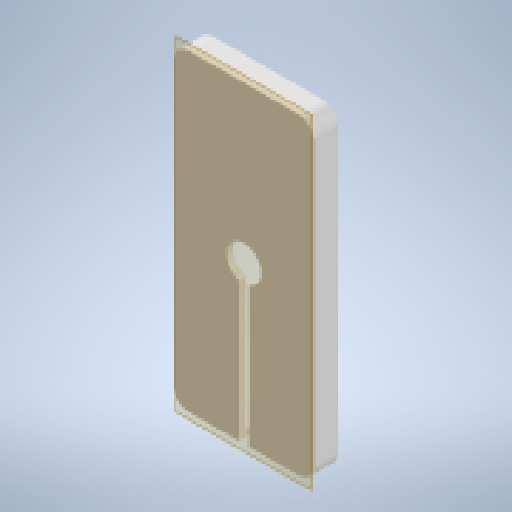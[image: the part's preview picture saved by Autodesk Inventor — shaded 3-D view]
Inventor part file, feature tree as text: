
AUTODESK INVENTOR PART (.ipt)
format: ipt  version: 2023 (Build 270158000, 158)  size: 202,752 bytes
history: native  units: mm
features: other x4, extrude x4, sketch x4, projected_geometry x3
ambient origin geometry x8: Origin, YZ Plane, XZ Plane, XY Plane, X Axis, Y Axis, Z Axis, Center Point
bodies: Solide1 (feature_tree)
feature tree (15):
  other  "Plan de construction1"
  extrude  "Extrusion1"  Depth=0.4mm
  extrude  "Extrusion2"  Depth=2.0mm
  extrude  "Extrusion3"  Depth=2.0mm TaperAngle=0.0deg
  extrude  "Extrusion4"  Depth=2.0mm
  sketch  "Esquisse1"
  other  "Référence1"
  sketch  "Esquisse2"
  projected_geometry  "Boucle projetée1"
  sketch  "Esquisse3"
  projected_geometry  "Boucle projetée2"
  sketch  "Esquisse4"
  projected_geometry  "Boucle projetée3"
  other  "Ensemble1"
  other  "BatterieHolder:1"
